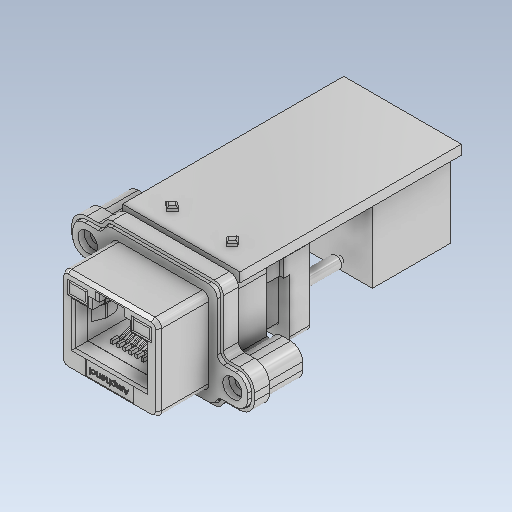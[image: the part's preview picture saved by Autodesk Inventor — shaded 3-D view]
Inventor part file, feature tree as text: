
AUTODESK INVENTOR PART (.ipt)
format: ipt  version: 2021 (Build 250183000, 183)  size: 973,824 bytes
history: native  units: mm
features: extrude x2, sketch x2, other x1
ambient origin geometry x8: Origin, YZ Plane, XZ Plane, XY Plane, X Axis, Y Axis, Z Axis, Center Point
bodies: Solid1 (feature_tree)
feature tree (5):
  extrude  "Extrusion1"  Depth=19.5mm
  extrude  "Extrusion2"  Depth=39.72mm
  sketch  "Sketch1"  dims[d0=16.0mm d1=19.5mm]
  sketch  "Sketch2"  dims[d2=0.5mm d3=39.72mm d4=1.6mm d5=0.0mm d6=16.0mm d7=0.0mm d8=13.0mm d9=13.5mm d10=0.0mm]
  other  "Boss-Extrude1"
